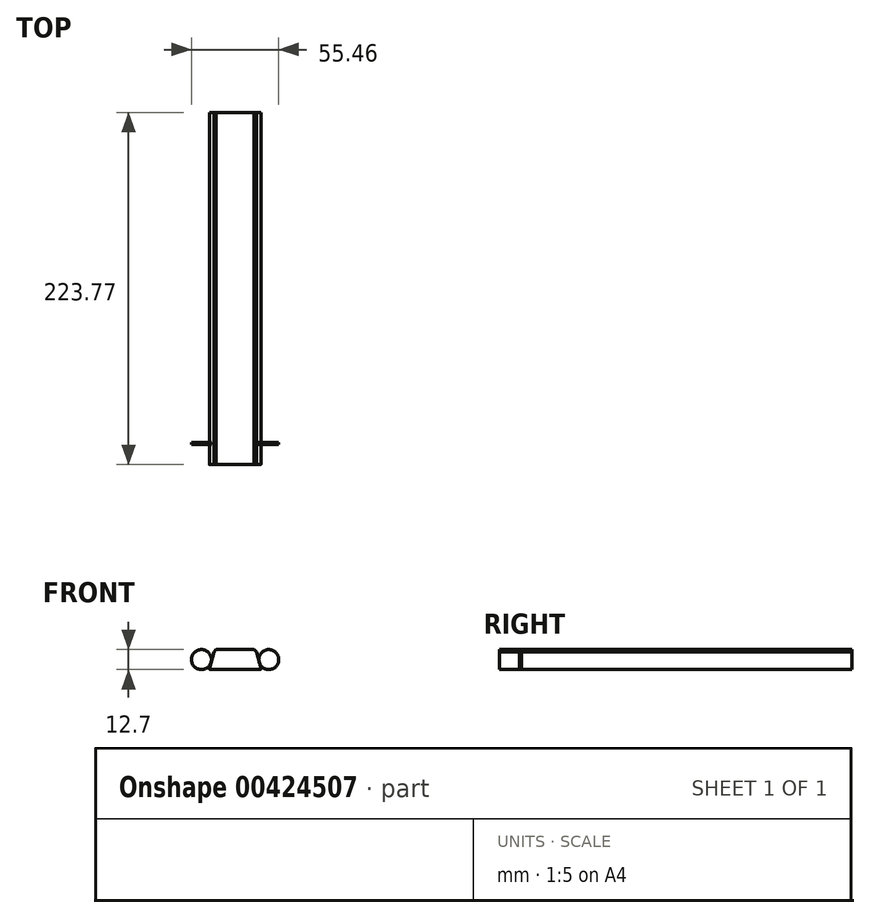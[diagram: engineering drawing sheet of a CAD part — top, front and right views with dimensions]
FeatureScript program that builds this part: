
annotation { "Feature Type Name" : "Feature", "Feature Type Description" : "" }
export const myFeature = defineFeature(function(context is Context, id is Id, definition is map)
    precondition{}
    {
        {
            var Q0;
            Q0=qCreatedBy(makeId("Front.planeOp"),FACE);
            var sketch = newSketch(context, id + "F0", { "sketchPlane" : qUnion([Q0])});
            skLineSegment(sketch, "E0", {"start": v(0.66, 0) * mm, "end": v(32.36, 0) * mm});
            skLineSegment(sketch, "E1", {"start": v(32.85, 0.64) * mm, "end": v(29.97, 11.38) * mm});
            skLineSegment(sketch, "E2", {"start": v(28.65, 12.7) * mm, "end": v(4.37, 12.7) * mm});
            skLineSegment(sketch, "E3", {"start": v(3.05, 11.38) * mm, "end": v(0.17, 0.64) * mm});
            skLineSegment(sketch, "E4", {"start": v(3.05, 11.38) * mm, "end": v(4.37, 12.7) * mm});
            skLineSegment(sketch, "E5", {"start": v(28.65, 12.7) * mm, "end": v(29.97, 11.38) * mm});
            skPoint(sketch, "E6.visualSharp", {"position": v(0, 0) * mm});
            skArc(sketch, "E6.filletArc", {"start": v(0.17, 0.64) * mm, "mid": v(0.26, 0.2) * mm, "end": v(0.66, 0) * mm});
            skPoint(sketch, "E7.visualSharp", {"position": v(33.02, 0) * mm});
            skArc(sketch, "E7.filletArc", {"start": v(32.36, 0) * mm, "mid": v(32.76, 0.2) * mm, "end": v(32.85, 0.64) * mm});
            skSolve(sketch);
        }
        {
            var Q0;
            Q0 = qSketchRegion(id + "F0", true);
            extrude(context, id + "F1", {"entities" : qUnion([Q0]), "depth" : 223.77 * mm});
        }
        {
            var Q0;
            Q0=makeQuery(id+"F1.opExtrude","CAP_FACE",FACE,{"disambiguationData":[OSD([sQuery(id+"F0.wireOp",EDGE,"E0"),sQuery(id+"F0.wireOp",EDGE,"E1"),sQuery(id+"F0.wireOp",EDGE,"E2"),sQuery(id+"F0.wireOp",EDGE,"E3"),sQuery(id+"F0.wireOp",EDGE,"E4"),sQuery(id+"F0.wireOp",EDGE,"E5"),sQuery(id+"F0.wireOp",EDGE,"E6.filletArc"),sQuery(id+"F0.wireOp",EDGE,"E7.filletArc")])],"isStart":false});
            cPlane(context, id + "F2", {"entities" : qUnion([Q0]), "cplaneType" : CPlaneType.OFFSET, "offset" : 12.7 * mm, "oppositeDirection" : true, "width" : 152.4 * mm, "height" : 152.4 * mm});
        }
        {
            var Q0;
            Q0=qCreatedBy(id+"F2.planeOp",FACE);
            var sketch = newSketch(context, id + "F3", { "sketchPlane" : qUnion([Q0])});
            skCircle(sketch, "E8", {"center": v(37.9, 6.35) * mm, "radius": 6.35 * mm});
            skLineSegment(sketch, "E9", {"start": v(16.51, 24.56) * mm, "end": v(16.51, -9.41) * mm});
            skCircle(sketch, "E10.MirrorC", {"center": v(-4.87, 6.35) * mm, "radius": 6.35 * mm});
            skSolve(sketch);
        }
        {
            var Q0;
            Q0 = qSketchRegion(id + "F3", true);
            extrude(context, id + "F4", {"entities" : qUnion([Q0]), "operationType" : NewBodyOperationType.ADD, "oppositeDirection" : true, "depth" : 1.27 * mm});
        }
    });
